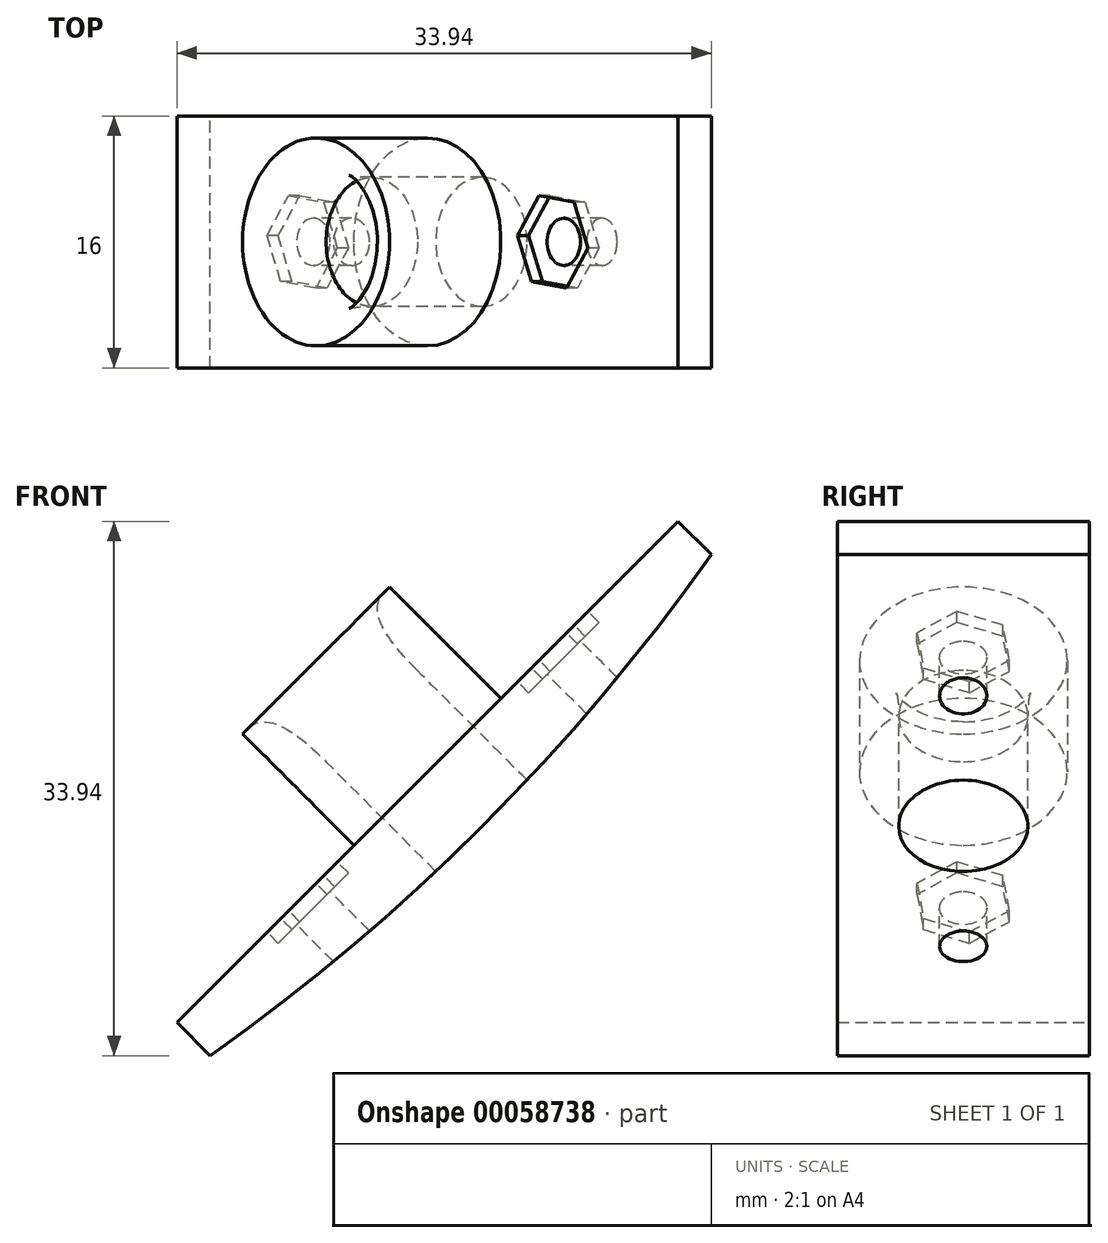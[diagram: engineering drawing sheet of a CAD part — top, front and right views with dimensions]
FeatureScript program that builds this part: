
annotation { "Feature Type Name" : "Feature", "Feature Type Description" : "" }
export const myFeature = defineFeature(function(context is Context, id is Id, definition is map)
    precondition{}
    {
        {
            var Q0;
            Q0=qCreatedBy(makeId("Front.planeOp"),FACE);
            var sketch = newSketch(context, id + "F0", { "sketchPlane" : qUnion([Q0])});
            skCircle(sketch, "E0", {"center": v(0, 0) * mm, "radius": 133.5 * mm, "construction": true});
            skLineSegment(sketch, "E1", {"start": v(0, 0) * mm, "end": v(0, -133.5) * mm, "construction": true});
            skLineSegment(sketch, "E2", {"start": v(0, 0) * mm, "end": v(94.4, -94.4) * mm, "construction": true});
            skLineSegment(sketch, "E3", {"start": v(0, 0) * mm, "end": v(94.4, 94.4) * mm, "construction": true});
            skLineSegment(sketch, "E4", {"start": v(0, 0) * mm, "end": v(-94.4, -94.4) * mm, "construction": true});
            skLineSegment(sketch, "E5", {"start": v(108.96, -77.14) * mm, "end": v(106.84, -75.02) * mm});
            skLineSegment(sketch, "E6", {"start": v(77.14, -108.96) * mm, "end": v(75.02, -106.84) * mm});
            skLineSegment(sketch, "E7", {"start": v(75.02, -106.84) * mm, "end": v(106.84, -75.02) * mm});
            skArc(sketch, "E8", {"start": v(77.14, -108.96) * mm, "mid": v(94.4, -94.4) * mm, "end": v(108.96, -77.14) * mm});
            skSolve(sketch);
        }
        {
            var Q0;
            Q0 = qSketchRegion(id + "F0", true);
            extrude(context, id + "F1", {"entities" : qUnion([Q0]), "depth" : 16 * mm});
        }
        {
            var Q0;
            Q0=makeQuery(id+"F1.opExtrude","SWEPT_FACE",FACE,{"disambiguationData":[OSD([sQuery(id+"F0.wireOp",EDGE,"E7")])]});
            var sketch = newSketch(context, id + "F2", { "sketchPlane" : qUnion([Q0])});
            skLineSegment(sketch, "E9", {"start": v(16, 22.5) * mm, "end": v(0, -22.5) * mm, "construction": true});
            skLineSegment(sketch, "E10", {"start": v(0, 22.5) * mm, "end": v(8, 0) * mm, "construction": true});
            skLineSegment(sketch, "E11", {"start": v(8, 0) * mm, "end": v(16, -22.5) * mm, "construction": true});
            skLineSegment(sketch, "E12", {"start": v(8, 0) * mm, "end": v(0, 0) * mm, "construction": true});
            skLineSegment(sketch, "E13", {"start": v(0, 0) * mm, "end": v(0, -22.5) * mm, "construction": true});
            skLineSegment(sketch, "E14", {"start": v(0, 0) * mm, "end": v(16, -22.5) * mm, "construction": true});
            skLineSegment(sketch, "E15", {"start": v(0, 0) * mm, "end": v(16, 22.5) * mm, "construction": true});
            skCircle(sketch, "E16", {"center": v(8, 11.25) * mm, "radius": 1.5 * mm});
            skCircle(sketch, "E17", {"center": v(8, 0) * mm, "radius": 4.1 * mm});
            skCircle(sketch, "E18", {"center": v(8, -11.25) * mm, "radius": 1.5 * mm});
            skSolve(sketch);
        }
        {
            var Q0;
            Q0 = qSketchRegion(id + "F2", true);
            extrude(context, id + "F3", {"entities" : qUnion([Q0]), "operationType" : NewBodyOperationType.REMOVE, "endBound" : BoundingType.THROUGH_ALL, "oppositeDirection" : true, "depth" : 25 * mm});
        }
        {
            var Q0;
            Q0=makeQuery(id+"F1.opExtrude","SWEPT_FACE",FACE,{"disambiguationData":[OSD([sQuery(id+"F0.wireOp",EDGE,"E7")])]});
            var sketch = newSketch(context, id + "F4", { "sketchPlane" : qUnion([Q0])});
            skCircle(sketch, "E19.cCircle", {"center": v(8, 11.25) * mm, "radius": 2.75 * mm, "construction": true});
            skLineSegment(sketch, "E19.0", {"start": v(10.53, 9.33) * mm, "end": v(7.6, 8.1) * mm});
            skLineSegment(sketch, "E19.1", {"start": v(7.6, 8.1) * mm, "end": v(5.07, 10.02) * mm});
            skLineSegment(sketch, "E19.2", {"start": v(5.07, 10.02) * mm, "end": v(5.47, 13.17) * mm});
            skLineSegment(sketch, "E19.3", {"start": v(5.47, 13.17) * mm, "end": v(8.4, 14.4) * mm});
            skLineSegment(sketch, "E19.4", {"start": v(8.4, 14.4) * mm, "end": v(10.93, 12.48) * mm});
            skLineSegment(sketch, "E19.5", {"start": v(10.93, 12.48) * mm, "end": v(10.53, 9.33) * mm});
            skPoint(sketch, "E19.0.midPoint", {"position": v(9.06, 8.71) * mm});
            skCircle(sketch, "E20.cCircle", {"center": v(8, -11.25) * mm, "radius": 2.75 * mm, "construction": true});
            skPoint(sketch, "E20.cCircle.perimeterSnap0", {"position": v(6.33, 9.06) * mm});
            skLineSegment(sketch, "E20.0", {"start": v(7.6, -14.4) * mm, "end": v(5.07, -12.48) * mm});
            skLineSegment(sketch, "E20.1", {"start": v(5.07, -12.48) * mm, "end": v(5.47, -9.33) * mm});
            skLineSegment(sketch, "E20.2", {"start": v(5.47, -9.33) * mm, "end": v(8.4, -8.1) * mm});
            skLineSegment(sketch, "E20.3", {"start": v(8.4, -8.1) * mm, "end": v(10.93, -10.02) * mm});
            skLineSegment(sketch, "E20.4", {"start": v(10.93, -10.02) * mm, "end": v(10.53, -13.17) * mm});
            skLineSegment(sketch, "E20.5", {"start": v(10.53, -13.17) * mm, "end": v(7.6, -14.4) * mm});
            skPoint(sketch, "E20.0.midPoint", {"position": v(6.33, -13.44) * mm});
            skPoint(sketch, "E20.0.midPoint.positionSnap0", {"position": v(6.33, 9.06) * mm});
            skSolve(sketch);
        }
        {
            var Q0;
            Q0 = qSketchRegion(id + "F4", true);
            extrude(context, id + "F5", {"entities" : qUnion([Q0]), "operationType" : NewBodyOperationType.REMOVE, "oppositeDirection" : true, "depth" : 1 * mm});
        }
        {
            var Q0;
            Q0=makeQuery(id+"F1.opExtrude","CAP_FACE",FACE,{"disambiguationData":[OSD([sQuery(id+"F0.wireOp",EDGE,"E5"),sQuery(id+"F0.wireOp",EDGE,"E6"),sQuery(id+"F0.wireOp",EDGE,"E7"),sQuery(id+"F0.wireOp",EDGE,"E8")])],"isStart":false});
            var Q1;
            Q1=makeQuery(id+"F1.opExtrude","CAP_FACE",FACE,{"disambiguationData":[OSD([sQuery(id+"F0.wireOp",EDGE,"E5"),sQuery(id+"F0.wireOp",EDGE,"E6"),sQuery(id+"F0.wireOp",EDGE,"E7"),sQuery(id+"F0.wireOp",EDGE,"E8")])],"isStart":true});
            cPlane(context, id + "F6", {"entities" : qUnion([Q0, Q1]), "cplaneType" : CPlaneType.MID_PLANE, "offset" : 150 * mm, "width" : 150 * mm, "height" : 150 * mm});
        }
        {
            var Q0;
            Q0=qCreatedBy(id+"F6.planeOp",FACE);
            var sketch = newSketch(context, id + "F7", { "sketchPlane" : qUnion([Q0])});
            skLineSegment(sketch, "E21", {"start": v(90.93, -90.93) * mm, "end": v(83.86, -83.86) * mm, "construction": true});
            skLineSegment(sketch, "E22", {"start": v(93.83, -88.03) * mm, "end": v(86.76, -80.96) * mm, "construction": true});
            skLineSegment(sketch, "E23", {"start": v(93.83, -88.03) * mm, "end": v(90.93, -90.93) * mm, "construction": true});
            skLineSegment(sketch, "E24", {"start": v(86.76, -80.96) * mm, "end": v(88.17, -79.54) * mm, "construction": true});
            skLineSegment(sketch, "E25", {"start": v(88.17, -79.54) * mm, "end": v(88.52, -79.19) * mm});
            skLineSegment(sketch, "E26", {"start": v(88.52, -79.19) * mm, "end": v(95.6, -86.26) * mm});
            skLineSegment(sketch, "E27", {"start": v(95.6, -86.26) * mm, "end": v(93.83, -88.03) * mm});
            skFitSpline(sketch, "E28", {"points": [v(88.17, -79.54) * mm, v(90.3, -84.5) * mm], "startDerivative": vector(-3.76, -3.76) * mm, "endDerivative": vector(4.68, -4.68) * mm});
            skLineSegment(sketch, "E29", {"start": v(90.3, -84.5) * mm, "end": v(93.83, -88.03) * mm});
            skSolve(sketch);
        }
        {
            var Q0;
            Q0 = qSketchRegion(id + "F7", true);
            var Q1;
            Q1=sQuery(id+"F7.wireOp",EDGE,"E21");
            revolve(context, id + "F8", {"operationType" : NewBodyOperationType.ADD, "entities" : qUnion([Q0]), "axis" : qUnion([Q1]), "revolveType" : RevolveType.FULL});
        }
    });
